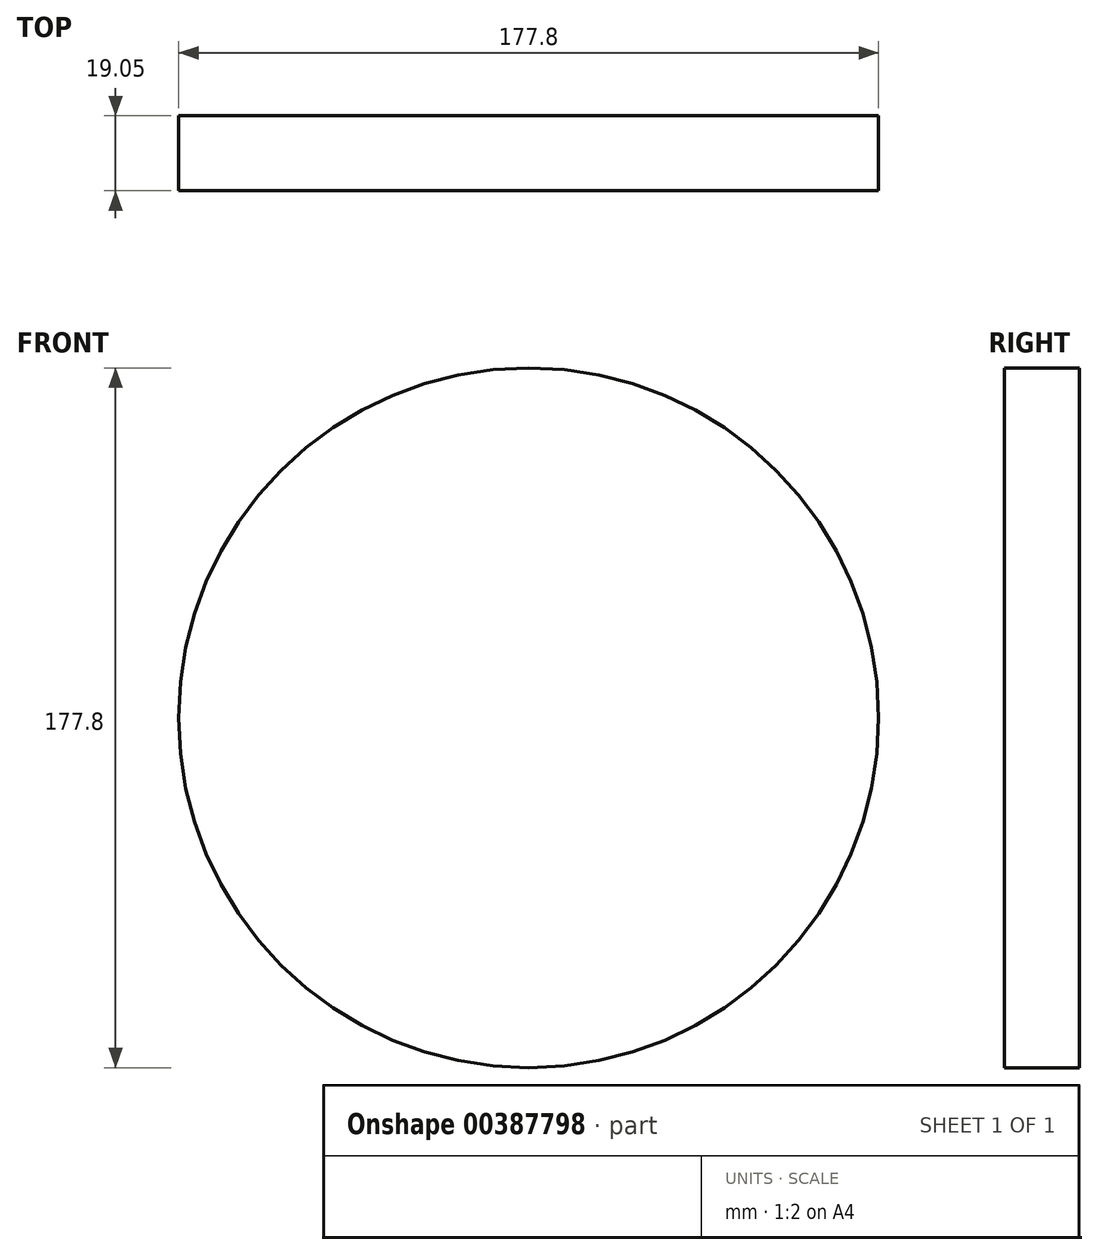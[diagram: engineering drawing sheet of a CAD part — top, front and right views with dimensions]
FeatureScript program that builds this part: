
annotation { "Feature Type Name" : "Feature", "Feature Type Description" : "" }
export const myFeature = defineFeature(function(context is Context, id is Id, definition is map)
    precondition{}
    {
        {
            var Q0;
            Q0=qCreatedBy(makeId("Front.planeOp"),FACE);
            var sketch = newSketch(context, id + "F0", { "sketchPlane" : qUnion([Q0])});
            skCircle(sketch, "E0", {"center": v(0, 0) * mm, "radius": 88.9 * mm});
            skSolve(sketch);
        }
        {
            var Q0;
            Q0=makeQuery(id+"F0.imprint","IMPRINT",FACE,{"disambiguationData":[TD([[makeQuery(id+"F0.imprint","IMPRINT",EDGE,{"derivedFrom":sQuery(id+"F0.wireOp",EDGE,"E0")}),1.0]])]});
            extrude(context, id + "F1", {"entities" : qUnion([Q0]), "depth" : 19.05 * mm});
        }
    });
